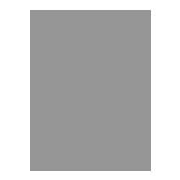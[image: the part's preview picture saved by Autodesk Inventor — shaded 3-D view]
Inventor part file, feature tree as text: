
AUTODESK INVENTOR PART (.ipt)
format: ipt  version: 2019.4 (Build 234330000, 330)  size: 112,128 bytes
history: native  units: mm (DEFAULTED — no unit token found)
features: other x4, plane x3, split x2, sketch x2
ambient origin geometry x8: Origin, YZ Plane, XZ Plane, XY Plane, X Axis, Y Axis, Z Axis, Center Point
bodies: Solid1 (feature_tree), Body (feature_tree)
feature tree (11):
  parser-record x1  (decoder bookkeeping rows leaked as tree rows — omitted from the tree; the rows remain in map.json)
  other  "Driven Length"
  other  "Start plane"
  other  "End plane"
  plane  "Work Plane8"
  split  "Split5"
  plane  "Work Plane9"
  split  "Split6"
  sketch  "Sketch3"  dims[d0=12.7mm]
  plane  "Work Plane3"
  sketch  "Sketch4"  dims[d1=12.7mm d2=190.5mm d3=0.0mm d4=6.35mm d5=6.35mm d6=6.35mm d7=196.85mm d8=90.0deg d9=190.5mm]
